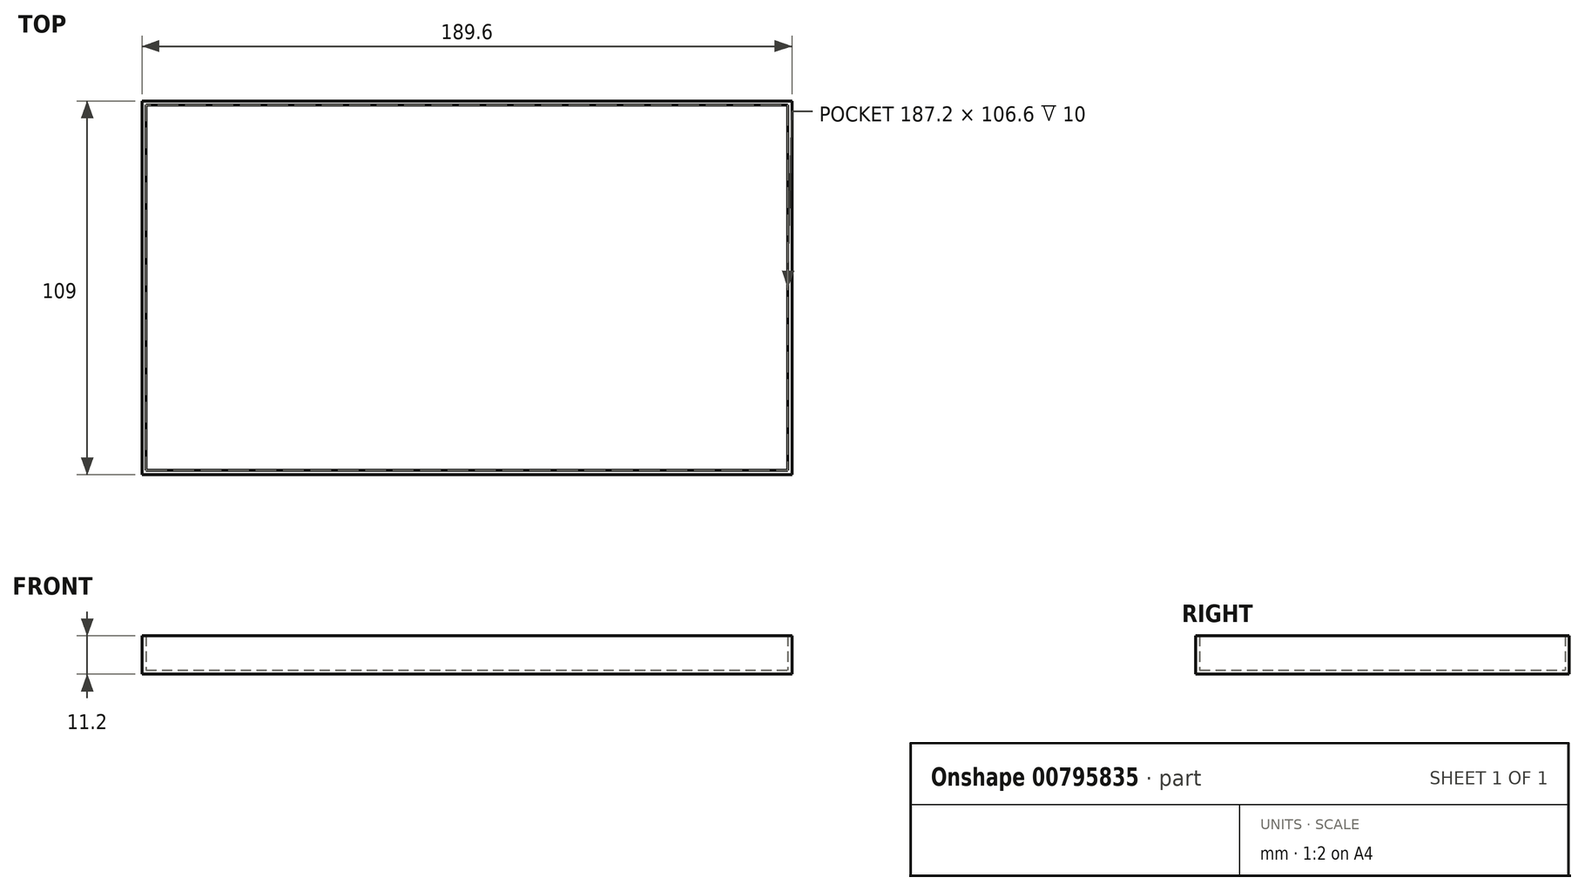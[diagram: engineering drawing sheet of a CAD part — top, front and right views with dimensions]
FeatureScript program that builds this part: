
annotation { "Feature Type Name" : "Feature", "Feature Type Description" : "" }
export const myFeature = defineFeature(function(context is Context, id is Id, definition is map)
    precondition{}
    {
        {
            var Q0;
            Q0=qCreatedBy(makeId("Top.planeOp"),FACE);
            var sketch = newSketch(context, id + "F0", { "sketchPlane" : qUnion([Q0])});
            skLineSegment(sketch, "E0", {"start": v(-120.46, -53.1) * mm, "end": v(69.14, -53.1) * mm});
            skLineSegment(sketch, "E1", {"start": v(-120.46, -53.1) * mm, "end": v(-120.46, 55.9) * mm});
            skLineSegment(sketch, "E2", {"start": v(-120.46, 55.9) * mm, "end": v(69.14, 55.9) * mm});
            skLineSegment(sketch, "E3", {"start": v(69.14, 55.9) * mm, "end": v(69.14, -53.1) * mm});
            skSolve(sketch);
        }
        {
            var Q0;
            Q0=makeQuery(id+"F0.imprint","IMPRINT",FACE,{"disambiguationData":[TD([[makeQuery(id+"F0.imprint","IMPRINT",EDGE,{"derivedFrom":sQuery(id+"F0.wireOp",EDGE,"E0")}),1.0]])]});
            extrude(context, id + "F1", {"entities" : qUnion([Q0]), "depth" : (10 + 1.2) * mm, "offsetDistance" : 25 * mm});
        }
        {
            var Q0;
            Q0=makeQuery(id+"F1.opExtrude","CAP_FACE",FACE,{"disambiguationData":[OSD([sQuery(id+"F0.wireOp",EDGE,"E0"),sQuery(id+"F0.wireOp",EDGE,"E1"),sQuery(id+"F0.wireOp",EDGE,"E2"),sQuery(id+"F0.wireOp",EDGE,"E3")])],"isStart":false});
            shell(context, id + "F2", {"entities" : qUnion([Q0]), "thickness" : 1.2 * mm});
        }
    });
